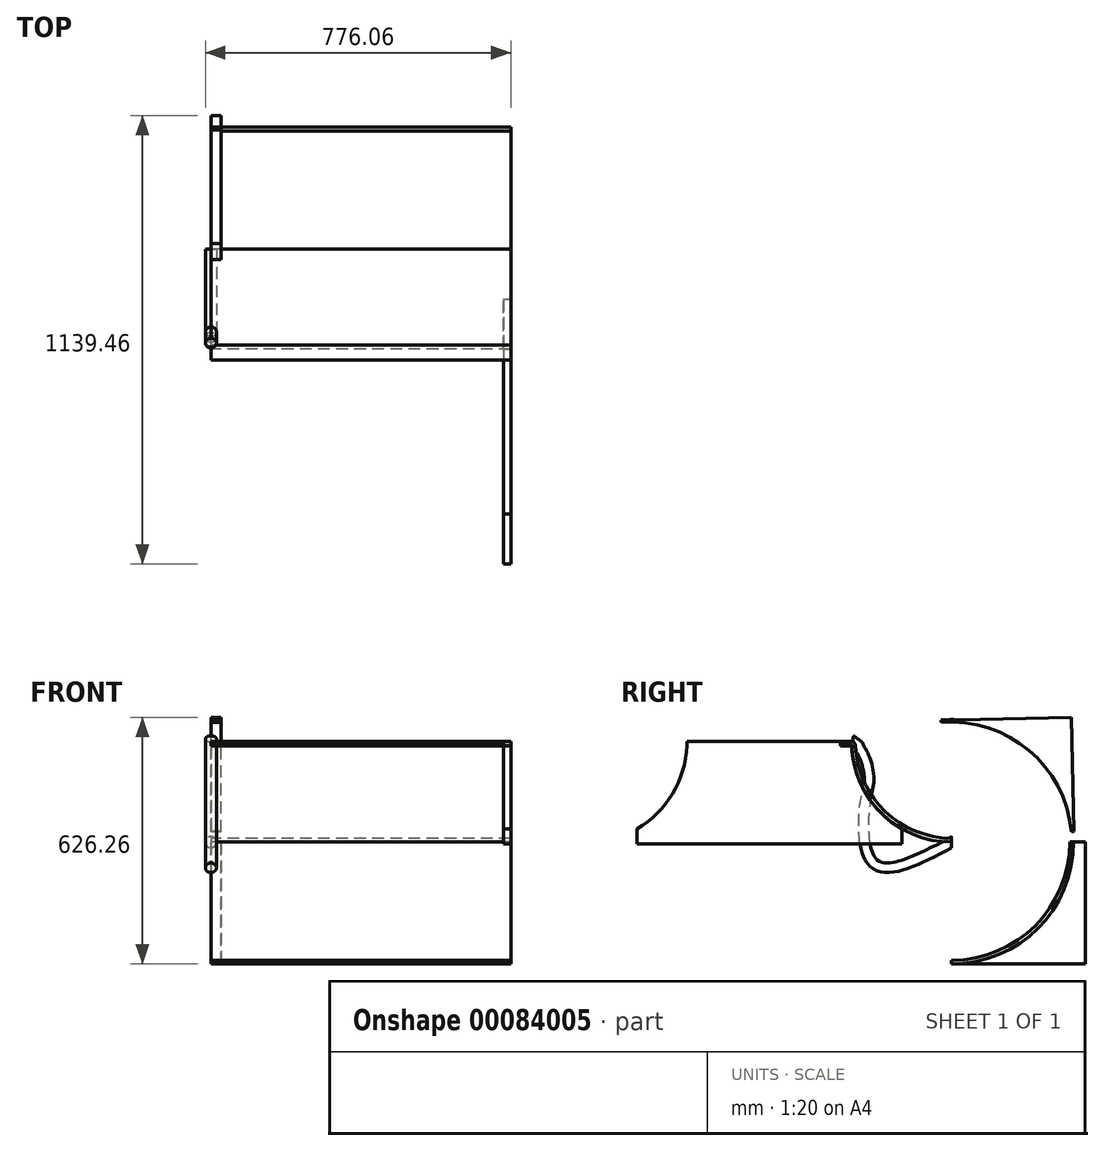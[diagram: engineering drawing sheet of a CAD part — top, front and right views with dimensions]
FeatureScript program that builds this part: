
annotation { "Feature Type Name" : "Feature", "Feature Type Description" : "" }
export const myFeature = defineFeature(function(context is Context, id is Id, definition is map)
    precondition{}
    {
        {
            var Q0;
            Q0=qCreatedBy(makeId("Right.planeOp"),FACE);
            var sketch = newSketch(context, id + "F0", { "sketchPlane" : qUnion([Q0])});
            skCircle(sketch, "E0", {"center": v(0, 0) * mm, "radius": 300.04 * mm});
            skCircle(sketch, "E1.0", {"center": v(0, 0) * mm, "radius": 309.56 * mm});
            skLineSegment(sketch, "E2", {"start": v(0, 0) * mm, "end": v(309.56, 0) * mm});
            skLineSegment(sketch, "E3", {"start": v(0, 0) * mm, "end": v(0, -309.56) * mm});
            skSolve(sketch);
        }
        {
            var Q0;
            {var subQ0=sQuery(id+"F0.wireOp",EDGE,"E2");var subQ1=sQuery(id+"F0.wireOp",EDGE,"E0");var subQ2=makeQuery(id+"F0.imprint","INTERSECT",VERTEX,{"derivedFrom":[subQ1,subQ0]});Q0=makeQuery(id+"F0.imprint","IMPRINT",FACE,{"disambiguationData":[TD([[makeQuery(id+"F0.imprint","IMPRINT",EDGE,{"disambiguationData":[TD([[subQ2,1.0]])],"derivedFrom":subQ1}),-1.0]])]});}
            extrude(context, id + "F1", {"entities" : qUnion([Q0]), "depth" : 762 * mm});
        }
        {
            var Q0;
            Q0=qCreatedBy(makeId("Right.planeOp"),FACE);
            var sketch = newSketch(context, id + "F2", { "sketchPlane" : qUnion([Q0])});
            skCircle(sketch, "E4", {"center": v(0, 0) * mm, "radius": 304.8 * mm});
            skCircle(sketch, "E5.0", {"center": v(0, 0) * mm, "radius": 311.15 * mm});
            skLineSegment(sketch, "E6", {"start": v(0, 0) * mm, "end": v(309.98, 27.01) * mm});
            skLineSegment(sketch, "E7", {"start": v(0, 0) * mm, "end": v(-27.01, 309.98) * mm});
            skSolve(sketch);
        }
        {
            var Q0;
            {var subQ0=sQuery(id+"F2.wireOp",EDGE,"E6");var subQ1=sQuery(id+"F2.wireOp",EDGE,"E4");var subQ2=makeQuery(id+"F2.imprint","INTERSECT",VERTEX,{"derivedFrom":[subQ1,subQ0]});Q0=makeQuery(id+"F2.imprint","IMPRINT",FACE,{"disambiguationData":[TD([[makeQuery(id+"F2.imprint","IMPRINT",EDGE,{"disambiguationData":[TD([[subQ2,-1.0]])],"derivedFrom":subQ1}),-1.0]])]});}
            extrude(context, id + "F3", {"entities" : qUnion([Q0]), "depth" : 25.4 * mm});
        }
        {
            var Q0;
            Q0=makeQuery(id+"F3.opExtrude","CAP_FACE",FACE,{"disambiguationData":[OSD([sQuery(id+"F2.wireOp",EDGE,"E4"),sQuery(id+"F2.wireOp",EDGE,"E5.0"),sQuery(id+"F2.wireOp",EDGE,"E6"),sQuery(id+"F2.wireOp",EDGE,"E7")])],"isStart":false});
            var sketch = newSketch(context, id + "F4", { "sketchPlane" : qUnion([Q0])});
            skLineSegment(sketch, "E8", {"start": v(309.98, 27.01) * mm, "end": v(304.1, 316.7) * mm});
            skLineSegment(sketch, "E9", {"start": v(304.1, 316.7) * mm, "end": v(-27.01, 309.98) * mm});
            skSolve(sketch);
        }
        {
            var Q0;
            {var subQ0=sQuery(id+"F4.wireOp",EDGE,"E8");Q0=makeQuery(id+"F4.imprint","IMPRINT",FACE,{"disambiguationData":[TD([[makeQuery(id+"F4.imprint","IMPRINT",EDGE,{"derivedFrom":subQ0}),1.0]])]});}
            extrude(context, id + "F5", {"entities" : qUnion([Q0]), "operationType" : NewBodyOperationType.ADD, "oppositeDirection" : true, "depth" : 25.4 * mm});
        }
        {
            var Q0;
            Q0=qCreatedBy(makeId("Right.planeOp"),FACE);
            var sketch = newSketch(context, id + "F6", { "sketchPlane" : qUnion([Q0])});
            skFitSpline(sketch, "E10", {"points": [v(0, 0) * mm, v(-198.25, -52.91) * mm, v(-219.94, 98.2) * mm, v(-209.91, 162.83) * mm, v(-225.18, 223.14) * mm, v(-237.9, 262.04) * mm], "startDerivative": vector(-889.46, -485.78) * mm, "endDerivative": vector(45.6, 353.68) * mm});
            skSolve(sketch);
        }
        {
            var Q0;
            Q0=qCreatedBy(makeId("Front.planeOp"),FACE);
            var sketch = newSketch(context, id + "F7", { "sketchPlane" : qUnion([Q0])});
            skCircle(sketch, "E11", {"center": v(0, 0) * mm, "radius": 14.06 * mm});
            skSolve(sketch);
        }
        {
            var Q0;
            Q0=makeQuery(id+"F7.imprint","IMPRINT",FACE,{"disambiguationData":[TD([[makeQuery(id+"F7.imprint","IMPRINT",EDGE,{"derivedFrom":sQuery(id+"F7.wireOp",EDGE,"E11")}),1.0]])]});
            var Q1;
            Q1=sQuery(id+"F6.wireOp",EDGE,"E10");
            sweep(context, id + "F8", {"profiles" : qUnion([Q0]), "path" : qUnion([Q1])});
        }
        {
            var Q0;
            Q0=makeQuery(id+"F1.opExtrude","CAP_FACE",FACE,{"disambiguationData":[OSD([sQuery(id+"F0.wireOp",EDGE,"E0"),sQuery(id+"F0.wireOp",EDGE,"E1.0"),sQuery(id+"F0.wireOp",EDGE,"E2"),sQuery(id+"F0.wireOp",EDGE,"E3")])],"isStart":true});
            var sketch = newSketch(context, id + "F9", { "sketchPlane" : qUnion([Q0])});
            skArc(sketch, "E12.0", {"start": v(0, -309.56) * mm, "mid": v(-218.9, -218.9) * mm, "end": v(-309.56, 0) * mm});
            skLineSegment(sketch, "E13", {"start": v(-309.56, 0) * mm, "end": v(-339.52, 0) * mm});
            skLineSegment(sketch, "E14", {"start": v(-339.52, 0) * mm, "end": v(-339.52, -309.56) * mm});
            skLineSegment(sketch, "E15", {"start": v(-339.52, -309.56) * mm, "end": v(0, -309.56) * mm});
            skSolve(sketch);
        }
        {
            var Q0;
            Q0 = qSketchRegion(id + "F9", true);
            extrude(context, id + "F10", {"entities" : qUnion([Q0]), "oppositeDirection" : true, "depth" : 25.4 * mm});
        }
        {
            var Q0;
            Q0=qCreatedBy(makeId("Right.planeOp"),FACE);
            var sketch = newSketch(context, id + "F11", { "sketchPlane" : qUnion([Q0])});
            skArc(sketch, "E16", {"start": v(-253.84, 244.98) * mm, "mid": v(-176.39, 71.24) * mm, "end": v(0, 0) * mm});
            skArc(sketch, "E17.0", {"start": v(-244.02, 245.02) * mm, "mid": v(-169.46, 78.19) * mm, "end": v(0, 9.81) * mm});
            skLineSegment(sketch, "E18", {"start": v(-253.84, 244.98) * mm, "end": v(-244.02, 245.02) * mm});
            skLineSegment(sketch, "E19", {"start": v(0, 9.81) * mm, "end": v(0, 0) * mm});
            skArc(sketch, "E20", {"start": v(-248.93, 245) * mm, "mid": v(-251.69, 249.58) * mm, "end": v(-256.72, 251.38) * mm, "construction": true});
            skLineSegment(sketch, "E21", {"start": v(-358.25, 251.38) * mm, "end": v(-256.72, 251.38) * mm, "construction": true});
            skArc(sketch, "E22.0", {"start": v(-244.02, 245.02) * mm, "mid": v(-248.25, 253.03) * mm, "end": v(-256.72, 256.23) * mm});
            skArc(sketch, "E23.0", {"start": v(-253.84, 244.98) * mm, "mid": v(-255.04, 246.24) * mm, "end": v(-256.72, 246.7) * mm});
            skLineSegment(sketch, "E24", {"start": v(-256.72, 256.23) * mm, "end": v(-256.72, 246.7) * mm});
            skLineSegment(sketch, "E25.bottom", {"start": v(-256.72, 256.23) * mm, "end": v(-282.12, 256.23) * mm});
            skLineSegment(sketch, "E25.top", {"start": v(-256.72, 246.7) * mm, "end": v(-282.12, 246.7) * mm});
            skLineSegment(sketch, "E25.right", {"start": v(-282.12, 256.23) * mm, "end": v(-282.12, 246.7) * mm});
            skSolve(sketch);
        }
        {
            var Q0;
            Q0 = qSketchRegion(id + "F11", true);
            extrude(context, id + "F12", {"entities" : qUnion([Q0]), "depth" : 762 * mm});
        }
        {
            var Q0;
            Q0=makeQuery(id+"F12.opExtrude","CAP_FACE",FACE,{"disambiguationData":[OSD([sQuery(id+"F11.wireOp",EDGE,"E16"),sQuery(id+"F11.wireOp",EDGE,"E17.0"),sQuery(id+"F11.wireOp",EDGE,"E19"),sQuery(id+"F11.wireOp",EDGE,"E22.0"),sQuery(id+"F11.wireOp",EDGE,"E23.0"),sQuery(id+"F11.wireOp",EDGE,"E24")])],"isStart":false});
            var sketch = newSketch(context, id + "F13", { "sketchPlane" : qUnion([Q0])});
            skPoint(sketch, "E26.orphan", {"position": v(0, 0) * mm});
            skLineSegment(sketch, "E27", {"start": v(-253.84, 244.98) * mm, "end": v(-253.84, -4.16) * mm});
            skLineSegment(sketch, "E28.0", {"start": v(-253.84, 244.98) * mm, "end": v(-253.84, 244.98) * mm});
            skLineSegment(sketch, "E29.bottom", {"start": v(-253.84, -4.16) * mm, "end": v(-463.39, -4.16) * mm});
            skArc(sketch, "E30.0", {"start": v(-253.84, 244.98) * mm, "mid": v(-176.39, 71.24) * mm, "end": v(0, 0) * mm});
            skLineSegment(sketch, "E31", {"start": v(0, 0) * mm, "end": v(0, 5.64) * mm});
            skLineSegment(sketch, "E32", {"start": v(-253.84, -4.16) * mm, "end": v(-126.84, -4.16) * mm});
            skLineSegment(sketch, "E33", {"start": v(-126.84, -4.16) * mm, "end": v(-126.84, 33.94) * mm});
            skLineSegment(sketch, "E34", {"start": v(-282.12, 256.23) * mm, "end": v(-463.39, 256.23) * mm});
            skLineSegment(sketch, "E35", {"start": v(-282.12, 256.23) * mm, "end": v(-282.12, 244.98) * mm});
            skPoint(sketch, "E36.orphan", {"position": v(-682.76, 245.02) * mm});
            skPoint(sketch, "E37.orphan", {"position": v(-672.94, -4.16) * mm});
            skLineSegment(sketch, "E38", {"start": v(-253.84, 244.98) * mm, "end": v(-282.12, 244.98) * mm});
            skLineSegment(sketch, "E39", {"start": v(-463.39, -4.16) * mm, "end": v(-463.39, 256.23) * mm});
            skLineSegment(sketch, "E40.MirrorCS", {"start": v(-799.94, -4.16) * mm, "end": v(-799.94, 33.94) * mm});
            skLineSegment(sketch, "E41.MirrorCS", {"start": v(-672.94, -4.16) * mm, "end": v(-463.39, -4.16) * mm});
            skLineSegment(sketch, "E42.MirrorCS", {"start": v(-644.66, 256.23) * mm, "end": v(-463.39, 256.23) * mm});
            skPoint(sketch, "E43.MirrorP", {"position": v(-253.84, -4.16) * mm});
            skLineSegment(sketch, "E44.MirrorCS", {"start": v(-672.94, 244.98) * mm, "end": v(-672.94, -4.16) * mm});
            skLineSegment(sketch, "E45.MirrorCS", {"start": v(-672.94, -4.16) * mm, "end": v(-799.94, -4.16) * mm});
            skArc(sketch, "E46.MirrorCS", {"start": v(-672.94, 244.98) * mm, "mid": v(-709.15, 123.04) * mm, "end": v(-799.94, 33.94) * mm});
            skLineSegment(sketch, "E47", {"start": v(-644.66, 256.23) * mm, "end": v(-672.94, 256.23) * mm});
            skLineSegment(sketch, "E48", {"start": v(-672.94, 244.98) * mm, "end": v(-672.94, 256.23) * mm});
            skPoint(sketch, "E48.endSnap0", {"position": v(-672.47, 256.23) * mm});
            skSolve(sketch);
        }
        {
            var Q0;
            Q0 = qSketchRegion(id + "F13", true);
            var Q1;
            Q1=makeQuery(id+"F13.imprint","IMPRINT",FACE,{"disambiguationData":[TD([[makeQuery(id+"F13.imprint","IMPRINT",EDGE,{"derivedFrom":sQuery(id+"F13.wireOp",EDGE,"E27")}),-1.0]])]});
            extrude(context, id + "F14", {"entities" : qUnion([Q0, Q1]), "oppositeDirection" : true, "depth" : 19.05 * mm});
        }
    });
